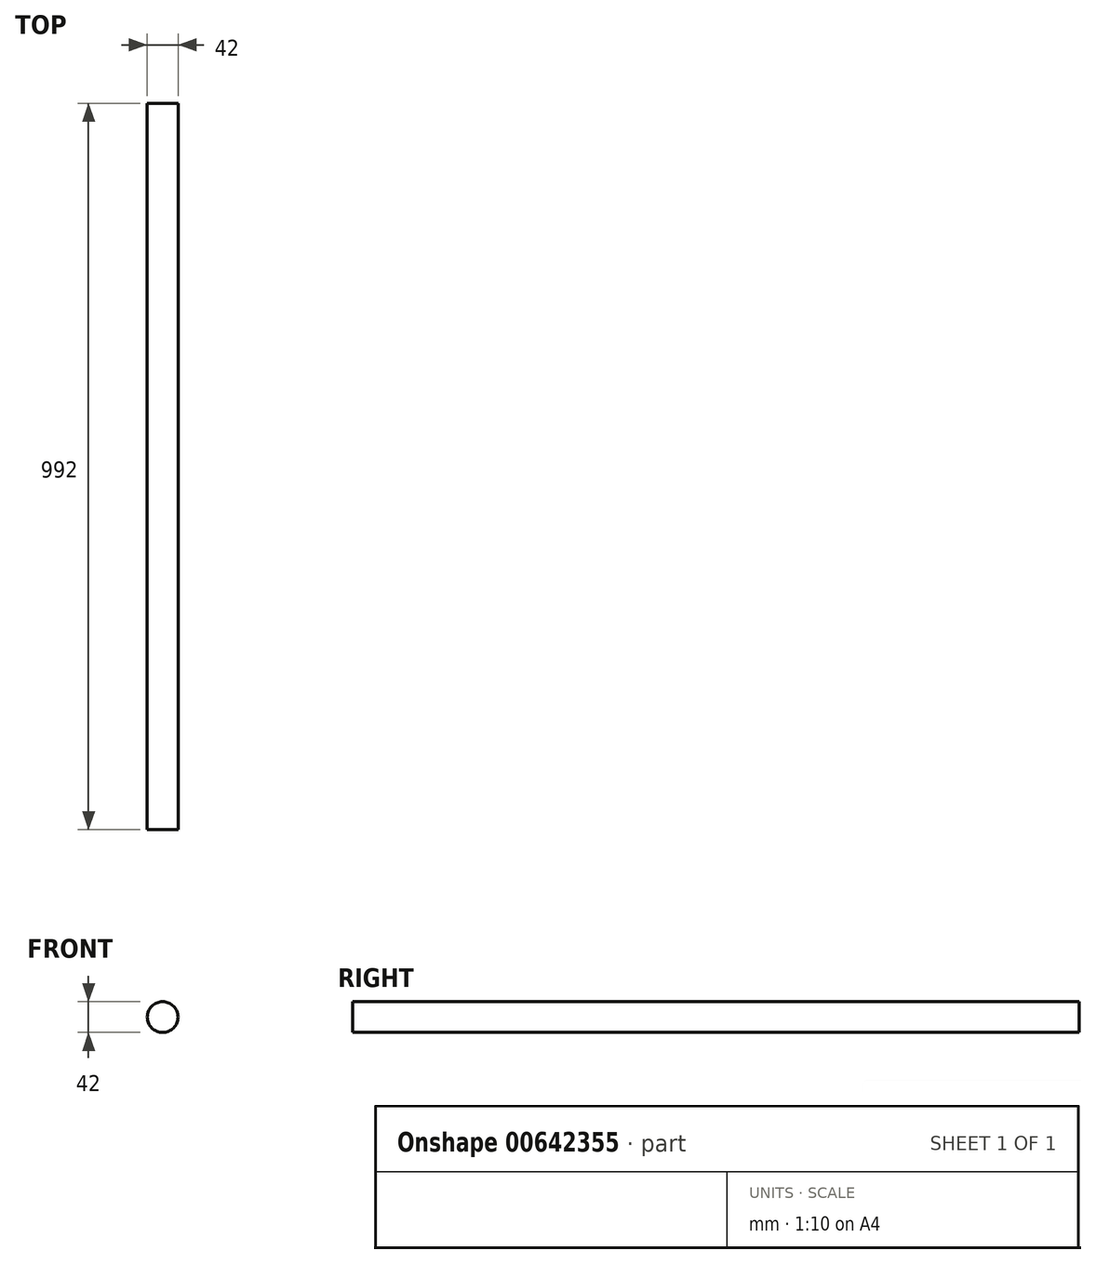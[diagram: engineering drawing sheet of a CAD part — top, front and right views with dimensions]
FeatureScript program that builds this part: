
annotation { "Feature Type Name" : "Feature", "Feature Type Description" : "" }
export const myFeature = defineFeature(function(context is Context, id is Id, definition is map)
    precondition{}
    {
        {
            var Q0;
            Q0=qCreatedBy(makeId("Front.planeOp"),FACE);
            var sketch = newSketch(context, id + "F0", { "sketchPlane" : qUnion([Q0])});
            skCircle(sketch, "E0", {"center": v(0, 0) * mm, "radius": 21 * mm});
            skSolve(sketch);
        }
        {
            var Q0;
            Q0=makeQuery(id+"F0.imprint","IMPRINT",FACE,{"disambiguationData":[TD([[makeQuery(id+"F0.imprint","IMPRINT",EDGE,{"derivedFrom":sQuery(id+"F0.wireOp",EDGE,"E0")}),1.0]])]});
            extrude(context, id + "F1", {"entities" : qUnion([Q0]), "depth" : (1000 - 8) * mm, "offsetDistance" : 25 * mm});
        }
    });
